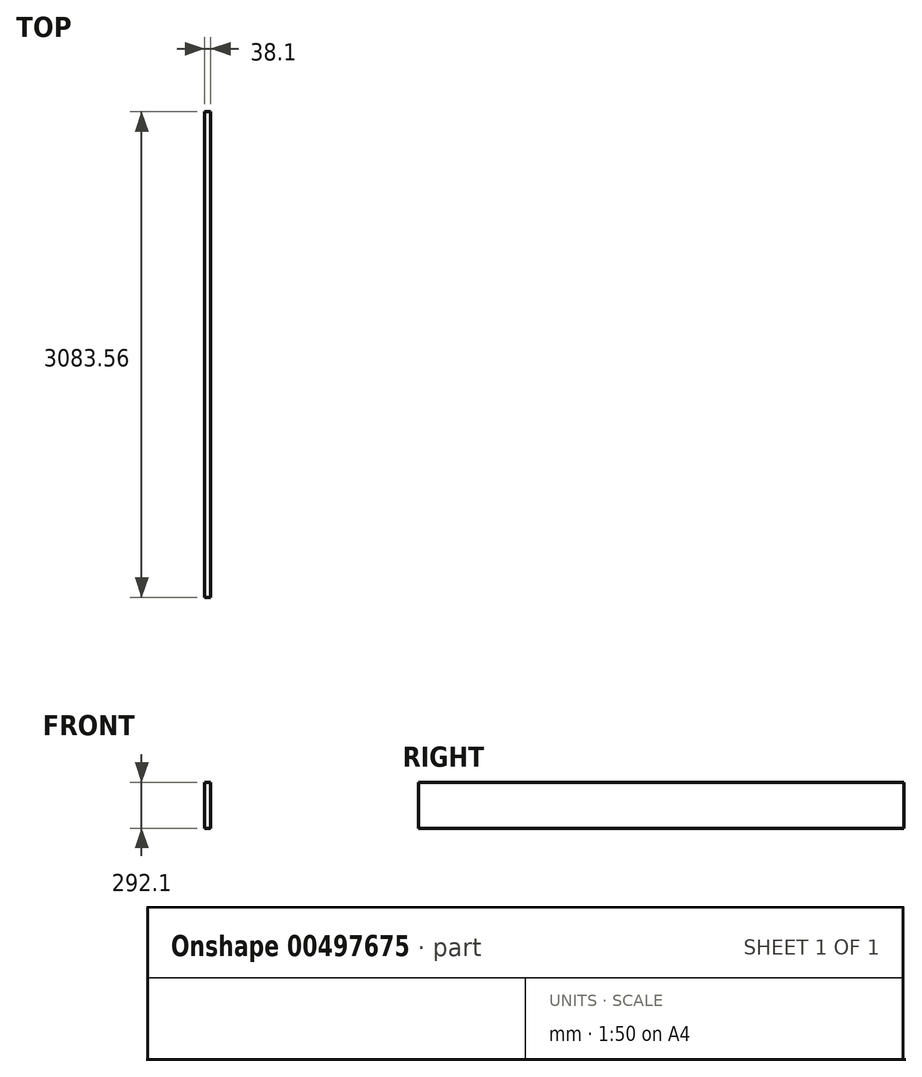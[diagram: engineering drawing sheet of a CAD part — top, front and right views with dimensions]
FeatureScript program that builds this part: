
annotation { "Feature Type Name" : "Feature", "Feature Type Description" : "" }
export const myFeature = defineFeature(function(context is Context, id is Id, definition is map)
    precondition{}
    {
        {
            var Q0;
            Q0=qCreatedBy(makeId("Front.planeOp"),FACE);
            var sketch = newSketch(context, id + "F0", { "sketchPlane" : qUnion([Q0])});
            skLineSegment(sketch, "E0.bottom", {"start": v(0, -6.32) * mm, "end": v(38.1, -6.32) * mm});
            skLineSegment(sketch, "E0.top", {"start": v(0, 285.78) * mm, "end": v(38.1, 285.78) * mm});
            skLineSegment(sketch, "E0.left", {"start": v(0, -6.32) * mm, "end": v(0, 285.78) * mm});
            skLineSegment(sketch, "E0.right", {"start": v(38.1, -6.32) * mm, "end": v(38.1, 285.78) * mm});
            skSolve(sketch);
        }
        {
            var Q0;
            Q0 = qSketchRegion(id + "F0", true);
            extrude(context, id + "F1", {"entities" : qUnion([Q0]), "depth" : 3083.56 * mm});
        }
    });
